# Revit family: Commercial_Rainshower_System-GROHE-Eurocube-29432 _Series.rfaxxx
name_source: partatom
category: Plumbing Fixtures
units: mm (PartAtom-declared; Revit-internal decimal feet)

## family parameters
Cut with Voids When Loaded = No
Host = Face
OmniClass Number = 23.45.05.14.17
OmniClass Title = Showers
Part Type = Normal
Room Calculation Point = No
Round Connector Dimension = Use Diameter
Shared = Yes

## types (4) — shared parameters
26 570- Rainshower™ 310 Mono showerhead, 1 spray, 1.75gpm = Yes
26 632- Rainshower™ 15” shower arm with square flange = Yes
26 634- Euphoria® Cube wall union = Yes
26 867- Euphoria® Cube hand shower, 1 spray, 1.75gpm = Yes
27 892- Euphoria® Cube 24” Shower Bar = Yes
28 417- RotaFlex Metal Longlife metallic hose = Yes
29 422- Eurocube® Pressure Balance Valve Trim with 2-Way Diverter = Yes
35 117- GrohSafe™ 3.0 Pressure Balance Rough Valve with Integrated Diverter = Yes
ASME A112.18.1/CSA B125.1/ASSE 1016 = Yes
ASSE 1016 = Yes
Assembly Code = D2010710
CEC Compliant = Yes
CW Connection = Yes
CWFU = 3
CalGreen Compliant = Yes
Cold Water Connection Diameter = 1/2"
Connection Diameter = 1/2"
Default Elevation = 0"
Description = EUROCUBE- Pressure Balance Rainshower Set
Double check valves = Included
EPA WaterSense® Certified = Yes
Flow Rate = Max. 1.75gpm (6.6L/min)
HW Connection = Yes
HWFU = 3
Height- Diverter = 48"
Height- Showerhead = 78"
Hot Water Connection Diameter = 1/2"
IAPMO Compliance = Massachusetts Plumbing Board Approved, Energy Policy Act of 1992, CSA B125.16
Installation Type = Wall Mounted
Manufacturer = GROHE
Price = Prices may vary. Please consult Manufacturer Representative for most up-to-date price list.
Tempered Water Connection = Yes
URL = https://www.grohe.us
Vent Connection = No
WFU = 4
Waste Connection = No

## per-type parameters (varying)
| type | Finish | Material |
| 29432000 | Metal-Grohe-000-StarLight Chrome | Metal-Grohe-000-StarLight Chrome |
| 29432A00 | Metal-Grohe-A00-Hard Graphite | Metal-Grohe-A00-Hard Graphite |
| 29432EN0 | Metal-Grohe-EN0-Brushed Nickel Infinity Finish | Metal-Grohe-EN0-Brushed Nickel Infinity Finish |
| 29432GN0 | Metal-Grohe-GN0-Brushed Cool Sunrise | Metal-Grohe-GN0-Brushed Cool Sunrise |

note: column(s) folded — value = type name in every type: Model

## geometry (parser evidence)
native form markers: Sweep x16
no freeform markers — native parametric forms only
